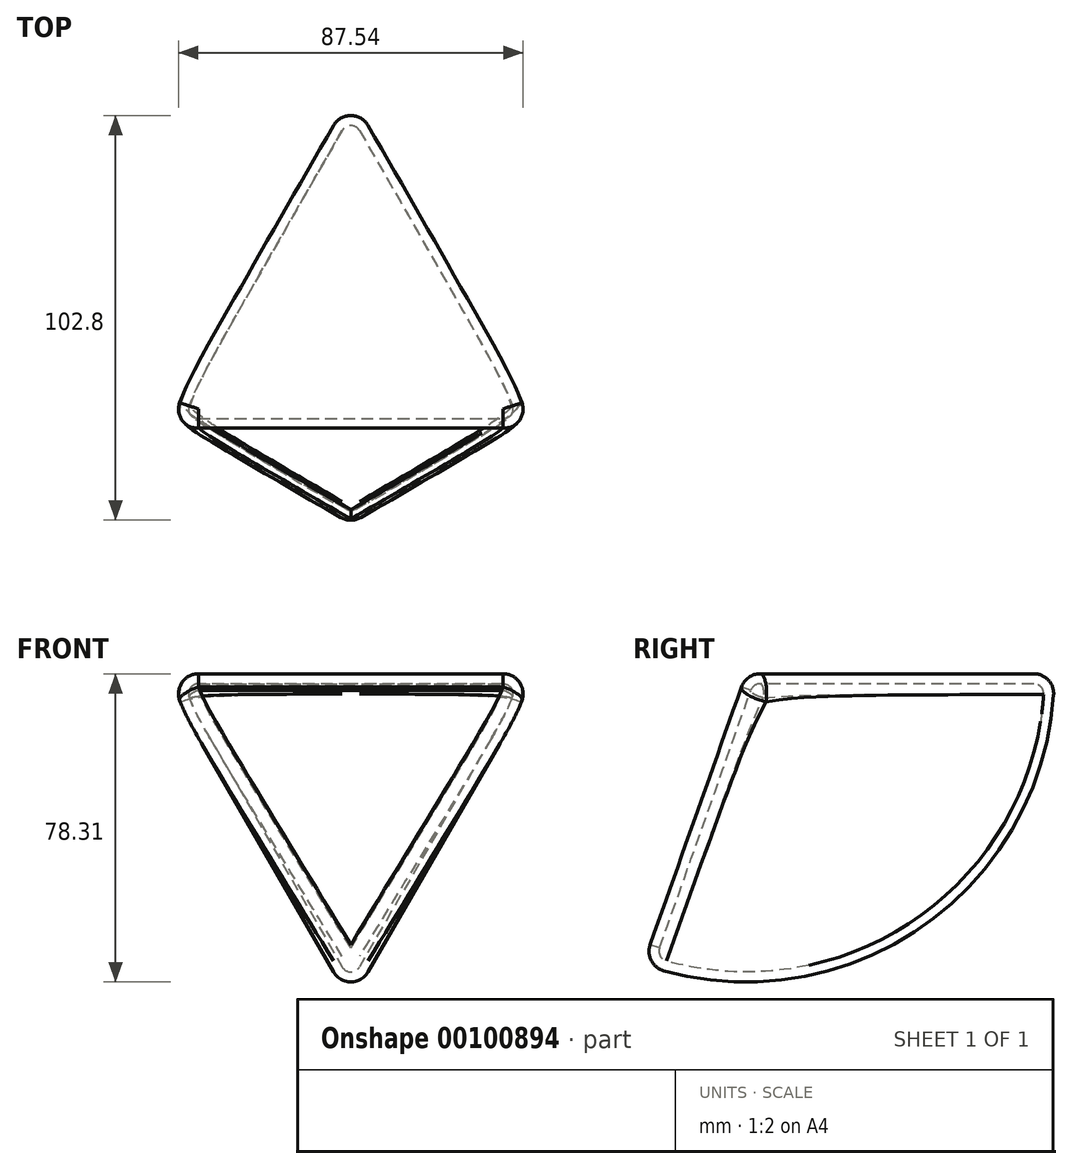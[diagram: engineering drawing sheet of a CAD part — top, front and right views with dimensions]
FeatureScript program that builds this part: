
annotation { "Feature Type Name" : "Feature", "Feature Type Description" : "" }
export const myFeature = defineFeature(function(context is Context, id is Id, definition is map)
    precondition{}
    {
        {
            var Q0;
            Q0=qCreatedBy(makeId("Top.planeOp"),FACE);
            var sketch = newSketch(context, id + "F0", { "sketchPlane" : qUnion([Q0])});
            skCircle(sketch, "E0.cCircle", {"center": v(0, 0) * mm, "radius": 27.8 * mm, "construction": true});
            skLineSegment(sketch, "E0.0", {"start": v(-48.14, -27.8) * mm, "end": v(0, 55.6) * mm});
            skLineSegment(sketch, "E0.1", {"start": v(0, 55.6) * mm, "end": v(48.14, -27.8) * mm});
            skLineSegment(sketch, "E0.2", {"start": v(48.14, -27.8) * mm, "end": v(-48.14, -27.8) * mm});
            skPoint(sketch, "E0.0.midPoint", {"position": v(-24.07, 13.9) * mm});
            skSolve(sketch);
        }
        {
            var Q0;
            Q0=makeQuery(id+"F0.imprint","IMPRINT",FACE,{"disambiguationData":[TD([[makeQuery(id+"F0.imprint","IMPRINT",EDGE,{"derivedFrom":sQuery(id+"F0.wireOp",EDGE,"E0.0")}),-1.0]])]});
            var Q1;
            Q1=sQuery(id+"F0.wireOp",EDGE,"E0.2");
            revolve(context, id + "F1", {"entities" : qUnion([Q0]), "axis" : qUnion([Q1]), "revolveType" : RevolveType.ONE_DIRECTION, "angle" : 109.5 * degree});
        }
        {
            var Q0;
            Q0=makeQuery(id+"F1.opRevolve","CAP_EDGE",EDGE,{"disambiguationData":[OSD([sQuery(id+"F0.wireOp",EDGE,"E0.2")])],"isStart":true});
            var Q1;
            Q1=makeQuery(id+"F1.opRevolve","CAP_EDGE",EDGE,{"disambiguationData":[OSD([sQuery(id+"F0.wireOp",EDGE,"E0.0")])],"isStart":true});
            var Q2;
            Q2=makeQuery(id+"F1.opRevolve","CAP_EDGE",EDGE,{"disambiguationData":[OSD([sQuery(id+"F0.wireOp",EDGE,"E0.1")])],"isStart":true});
            var Q3;
            Q3=makeQuery(id+"F1.opRevolve","CAP_EDGE",EDGE,{"disambiguationData":[OSD([sQuery(id+"F0.wireOp",EDGE,"E0.1")])],"isStart":false});
            var Q4;
            Q4=makeQuery(id+"F1.opRevolve","CAP_EDGE",EDGE,{"disambiguationData":[OSD([sQuery(id+"F0.wireOp",EDGE,"E0.0")])],"isStart":false});
            var Q5;
            Q5=makeQuery(id+"F1.opRevolve","SWEPT_EDGE",EDGE,{"disambiguationData":[OSD([sQuery(id+"F0.wireOp",EDGE,"E0.0"),sQuery(id+"F0.wireOp",EDGE,"E0.1")])]});
            fillet(context, id + "F2", {"entities" : qUnion([Q0, Q1, Q2, Q3, Q4, Q5]), "radius" : 5.08 * mm, "tangentPropagation" : true, "allowEdgeOverflow" : false});
        }
        {
            var Q0;
            Q0=makeQuery(id+"F1.opRevolve","CAP_FACE",FACE,{"disambiguationData":[OSD([sQuery(id+"F0.wireOp",EDGE,"E0.0"),sQuery(id+"F0.wireOp",EDGE,"E0.1"),sQuery(id+"F0.wireOp",EDGE,"E0.2")])],"isStart":false});
            shell(context, id + "F3", {"entities" : qUnion([Q0]), "thickness" : 2.54 * mm});
        }
    });
